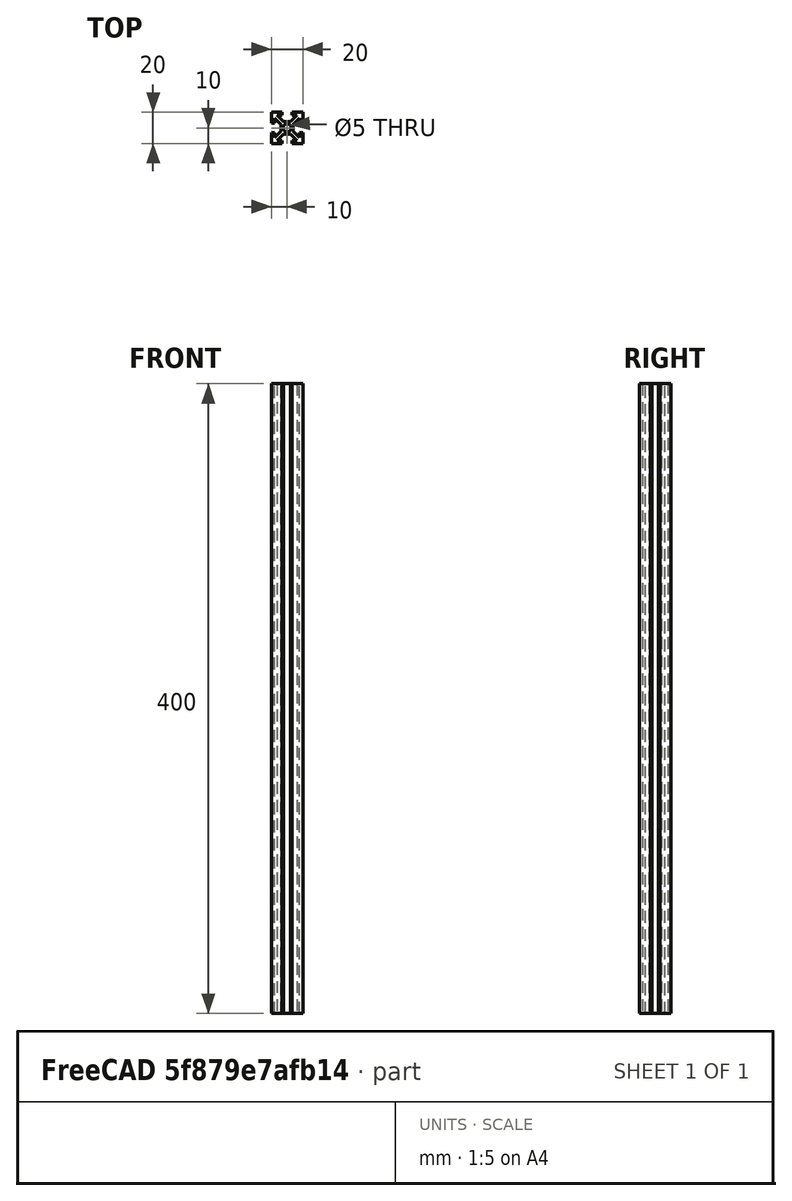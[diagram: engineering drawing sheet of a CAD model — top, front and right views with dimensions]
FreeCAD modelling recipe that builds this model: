
FCSTD DOCUMENT  (FreeCAD 1.0R39109 (Git))
Label: T-Slot_20_length
License: All rights reserved
LicenseURL: http://en.wikipedia.org/wiki/All_rights_reserved
objects: Sketcher::SketchObject×3, PartDesign::Pocket×2, TechDraw::DrawProjGroupItem×2, TechDraw::DrawViewDimension×2, PartDesign::Pad×1, PartDesign::Body×1, TechDraw::DrawSVGTemplate×1, TechDraw::DrawProjGroup×1, TechDraw::DrawPage×1
note: 19 computed .brp shape members not serialized (recipe doc carries the construction recipe); baked Part::Feature solids carry a one-line shape summary decoded from their .brp

FEATURE [Sketcher::SketchObject] Sketch
  ArcFitTolerance = 0
  AttachmentSupport = -> [XY_Plane]
  FullyConstrained = true
  MakeInternals = false
  MapMode = 5
  sketch-geometry (4):
    g0: LineSegment StartX=-10 StartY=10 StartZ=0 EndX=10 EndY=10 EndZ=0
    g1: LineSegment StartX=10 StartY=10 StartZ=0 EndX=10 EndY=-10 EndZ=0
    g2: LineSegment StartX=10 StartY=-10 StartZ=0 EndX=-10 EndY=-10 EndZ=0
    g3: LineSegment StartX=-10 StartY=-10 StartZ=0 EndX=-10 EndY=10 EndZ=0
  constraints (10):
    c: Coincident(g0,g1)
    c: Coincident(g1,g2)
    c: Coincident(g2,g3)
    c: Coincident(g3,g0)
    c: Horizontal(g0)
    c: Vertical(g1)
    c: Symmetric(g2,g1,g-2)
    c: Symmetric(g0,g2,g-1)
    c: Equal(g3,g2)
    c: Distance(g0) = 20
FEATURE [PartDesign::Pad] Pad  label="Change Length Here!"
  AllowMultiFace = false
  Direction = (0,0,1)
  Length = 400
  Length2 = 100
  Profile = -> Sketch
  ReferenceAxis = -> Sketch [N_Axis]
  Refine = true
  Suppressed = false
  Type = 0
FEATURE [Sketcher::SketchObject] Sketch001
  ArcFitTolerance = 0
  AttachmentSupport = -> [Pad]
  ExternalGeometry = -> [Pad]
  FullyConstrained = false
  MakeInternals = false
  MapMode = 5
  Placement = pos=(0,0,400) rot=(0,0,1;0rad)
  sketch-geometry (23):
    g0: LineSegment StartX=-3.1 StartY=10 StartZ=0 EndX=3.1 EndY=10 EndZ=0
    g1: LineSegment StartX=3.1 StartY=10 StartZ=0 EndX=3.1 EndY=8 EndZ=0
    g2: LineSegment [constr] StartX=3.1 StartY=8 StartZ=0 EndX=-3.1 EndY=8 EndZ=0
    g3: LineSegment StartX=-3.1 StartY=8 StartZ=0 EndX=-3.1 EndY=10 EndZ=0
    g4: LineSegment StartX=-3.1 StartY=8 StartZ=0 EndX=-6.23223 EndY=8 EndZ=0
    g5: LineSegment StartX=-6.23223 StartY=8 StartZ=0 EndX=-2.13223 EndY=3.9 EndZ=0
    g6: LineSegment StartX=-2.13223 StartY=3.9 StartZ=0 EndX=2.13223 EndY=3.9 EndZ=0
    g7: LineSegment StartX=2.13223 StartY=3.9 StartZ=0 EndX=6.23223 EndY=8 EndZ=0
    g8: LineSegment StartX=6.23223 StartY=8 StartZ=0 EndX=3.1 EndY=8 EndZ=0
    g9: LineSegment [constr] StartX=-3.9 StartY=3.9 StartZ=0 EndX=3.9 EndY=3.9 EndZ=0
    g10: LineSegment [constr] StartX=3.9 StartY=3.9 StartZ=0 EndX=3.9 EndY=-3.9 EndZ=0
    g11: LineSegment [constr] StartX=3.9 StartY=-3.9 StartZ=0 EndX=-3.9 EndY=-3.9 EndZ=0
    g12: LineSegment [constr] StartX=-3.9 StartY=-3.9 StartZ=0 EndX=-3.9 EndY=3.9 EndZ=0
    g13: Circle CenterX=0 CenterY=0 CenterZ=0 NormalX=0 NormalY=0 NormalZ=1 AngleXU=0 Radius=2.5
    g14: LineSegment [constr] StartX=3.9 StartY=3.9 StartZ=0 EndX=3.01612 EndY=4.78388 EndZ=0
    g15: LineSegment StartX=-3.1 StartY=-8 StartZ=0 EndX=-6.23223 EndY=-8 EndZ=0
    g16: LineSegment StartX=6.23223 StartY=-8 StartZ=0 EndX=3.1 EndY=-8 EndZ=0
    g17: LineSegment StartX=3.1 StartY=-10 StartZ=0 EndX=3.1 EndY=-8 EndZ=0
    g18: LineSegment StartX=-3.1 StartY=-10 StartZ=0 EndX=3.1 EndY=-10 EndZ=0
    g19: LineSegment StartX=-3.1 StartY=-8 StartZ=0 EndX=-3.1 EndY=-10 EndZ=0
    g20: LineSegment StartX=-6.23223 StartY=-8 StartZ=0 EndX=-2.13223 EndY=-3.9 EndZ=0
    g21: LineSegment StartX=-2.13223 StartY=-3.9 StartZ=0 EndX=2.13223 EndY=-3.9 EndZ=0
    g22: LineSegment StartX=2.13223 StartY=-3.9 StartZ=0 EndX=6.23223 EndY=-8 EndZ=0
  constraints (55):
    c: Coincident(g0,g1)
    c: Coincident(g1,g2)
    c: Coincident(g2,g3)
    c: Coincident(g3,g0)
    c: Horizontal(g2)
    c: Vertical(g1)
    c: Vertical(g3)
    c: PointOnObject(g0,g-3)
    c: Symmetric(g0,g0,g-2)
    c: Distance(g0) = 6.2
    c: Distance(g3) = 2
    c: Coincident(g3,g4)
    c: Horizontal(g4)
    c: Coincident(g4,g5)
    c: Coincident(g5,g6)
    c: Coincident(g6,g7)
    c: Coincident(g7,g8)
    c: Coincident(g8,g1)
    c: Horizontal(g8)
    c: Symmetric(g5,g6,g-2)
    c: Equal(g4,g8)
    c: Coincident(g9,g10)
    c: Coincident(g10,g11)
    c: Coincident(g11,g12)
    c: Coincident(g12,g9)
    c: Horizontal(g9)
    c: Vertical(g12)
    c: Equal(g9,g12)
    c: Symmetric(g11,g10,g-2)
    c: Symmetric(g9,g10,g-1)
    c: Distance(g9) = 7.8
    c: Coincident(g13,g-1)
    c: Radius(g13) = 2.5
    c: DistanceY(g6,g0) = 6.1
    c: Coincident(g14,g9)
    c: PointOnObject(g14,g7)
    c: Perpendicular(g7,g14)
    c: Distance(g14) = 1.25
    c: Angle(g6,g5) = 2.35619
    c: Coincident(g18,g17)
    c: Coincident(g19,g18)
    c: Vertical(g17)
    c: Vertical(g19)
    c: Distance(g18) = 6.2
    c: Distance(g19) = 2
    c: Coincident(g19,g15)
    c: Horizontal(g15)
    c: Coincident(g15,g20)
    c: Coincident(g20,g21)
    c: Coincident(g21,g22)
    c: Coincident(g22,g16)
    c: Coincident(g16,g17)
    c: Horizontal(g16)
    c: Equal(g15,g16)
    c: Angle(g21,g20) = -2.35619
FEATURE [PartDesign::Pocket] Pocket  label="Top & Bottom Slots"
  AllowMultiFace = false
  BaseFeature = -> Pad
  Direction = (0,0,-1)
  Length = 5
  Length2 = 100
  Profile = -> Sketch001
  Refine = true
  Suppressed = false
  Type = 1
FEATURE [Sketcher::SketchObject] Sketch002
  ArcFitTolerance = 0
  AttachmentSupport = -> [Pocket]
  ExternalGeometry = -> [Pocket]
  FullyConstrained = false
  MakeInternals = false
  MapMode = 5
  Placement = pos=(0,0,0) rot=(1,0,0;3.14159rad)
  sketch-geometry (19):
    g0: LineSegment StartX=-10 StartY=-3.1 StartZ=0 EndX=-8 EndY=-3.1 EndZ=0
    g1: LineSegment [constr] StartX=-8 StartY=-3.1 StartZ=0 EndX=-8 EndY=3.1 EndZ=0
    g2: LineSegment StartX=-8 StartY=3.1 StartZ=0 EndX=-10 EndY=3.1 EndZ=0
    g3: LineSegment StartX=-10 StartY=3.1 StartZ=0 EndX=-10 EndY=-3.1 EndZ=0
    g4: LineSegment StartX=-8 StartY=-3.1 StartZ=0 EndX=-8 EndY=-6.23223 EndZ=0
    g5: LineSegment StartX=-8 StartY=-6.23223 StartZ=0 EndX=-3.9 EndY=-2.13223 EndZ=0
    g6: LineSegment StartX=-3.9 StartY=-2.13223 StartZ=0 EndX=-3.9 EndY=2.13223 EndZ=0
    g7: LineSegment StartX=-3.9 StartY=2.13223 StartZ=0 EndX=-8 EndY=6.23223 EndZ=0
    g8: LineSegment StartX=-8 StartY=6.23223 StartZ=0 EndX=-8 EndY=3.1 EndZ=0
    g9: LineSegment [constr] StartX=-2.13223 StartY=3.9 StartZ=0 EndX=-3.9 EndY=2.13223 EndZ=0
    g10: LineSegment [constr] StartX=2.13223 StartY=3.9 StartZ=0 EndX=3.9 EndY=2.13223 EndZ=0
    g11: LineSegment StartX=3.9 StartY=-2.13223 StartZ=0 EndX=3.9 EndY=2.13223 EndZ=0
    g12: LineSegment StartX=8 StartY=-6.23223 StartZ=0 EndX=3.9 EndY=-2.13223 EndZ=0
    g13: LineSegment StartX=3.9 StartY=2.13223 StartZ=0 EndX=8 EndY=6.23223 EndZ=0
    g14: LineSegment StartX=8 StartY=6.23223 StartZ=0 EndX=8 EndY=3.1 EndZ=0
    g15: LineSegment StartX=8 StartY=3.1 StartZ=0 EndX=10 EndY=3.1 EndZ=0
    g16: LineSegment StartX=10 StartY=3.1 StartZ=0 EndX=10 EndY=-3.1 EndZ=0
    g17: LineSegment StartX=10 StartY=-3.1 StartZ=0 EndX=8 EndY=-3.1 EndZ=0
    g18: LineSegment StartX=8 StartY=-3.1 StartZ=0 EndX=8 EndY=-6.23223 EndZ=0
  constraints (43):
    c: Coincident(g0,g1)
    c: Coincident(g1,g2)
    c: Coincident(g2,g3)
    c: Coincident(g3,g0)
    c: Horizontal(g0)
    c: Horizontal(g2)
    c: Vertical(g1)
    c: PointOnObject(g0,g-3)
    c: Symmetric(g2,g0,g-1)
    c: Distance(g3) = 6.2
    c: Distance(g0) = 2
    c: Coincident(g0,g4)
    c: Vertical(g4)
    c: Coincident(g4,g5)
    c: Coincident(g5,g6)
    c: Coincident(g6,g7)
    c: Coincident(g7,g8)
    c: Coincident(g8,g2)
    c: Vertical(g8)
    c: Equal(g4,g8)
    c: Symmetric(g6,g5,g-1)
    c: DistanceX(g2,g6) = 6.1
    c: Angle(g6,g5) = 2.35619
    c: Coincident(g9,g-4)
    c: Perpendicular(g-4,g9)
    c: Coincident(g6,g9)
    c: Coincident(g15,g16)
    c: Coincident(g16,g17)
    c: Horizontal(g17)
    c: Horizontal(g15)
    c: Distance(g16) = 6.2
    c: Distance(g17) = 2
    c: Coincident(g17,g18)
    c: Vertical(g18)
    c: Coincident(g18,g12)
    c: Coincident(g12,g11)
    c: Coincident(g11,g13)
    c: Coincident(g13,g14)
    c: Coincident(g14,g15)
    c: Vertical(g14)
    c: Equal(g18,g14)
    c: Angle(g11,g12) = -2.35619
    c: Coincident(g11,g10)
FEATURE [PartDesign::Pocket] Pocket001  label="R&L Slots"
  AllowMultiFace = false
  BaseFeature = -> Pocket
  Direction = (0,0,1)
  Length = 5
  Length2 = 100
  Profile = -> Sketch002
  Refine = true
  Suppressed = false
  Type = 1
FEATURE [PartDesign::Body] Body  label="Tslot20_len"
  AllowCompound = false
  Group = -> [Sketch,Pad,Sketch001,Pocket,Sketch002,Pocket001]
  Origin = -> Origin
  Tip = -> Pocket001
FEATURE [TechDraw::DrawSVGTemplate] Template
  EditableTexts = approval_person=B. Hecate; creator=Djordje Vujic; date_of_issue=1/21/2025; document_type=Assembly Drawing; general_tolerances=ISO 2768-m; identification_number=DN; language_code=EN; part_material=Stainless steel Mat.No. 1.4301; revision_index=AAA; sheet_number=1 / 5; sheet_scale=1 : 2; title=T-Slot_20_length
  Height = 297
  Orientation = 0
  Template = D:/Program Files/FreeCAD 1.0/data/Mod/TechDraw/Templates/A4_Portrait_ISO5457_minimal.svg
  Width = 210
FEATURE [TechDraw::DrawProjGroupItem] ProjItem  label="Front"
  CoarseView = false
  Direction = (0,-1,0)
  Focus = 100
  HardHidden = false
  IsoCount = 0
  IsoHidden = false
  IsoVisible = false
  LockPosition = true
  Perspective = false
  Rotation = 0
  RotationVector = (1,0,0)
  Scale = 0.5
  ScaleType = 0
  ScrubCount = 1
  SeamHidden = false
  SeamVisible = false
  SmoothHidden = false
  SmoothVisible = true
  Source = -> [Body]
  Type = 0
  X = 0
  XDirection = (1,0,0)
  Y = 0
FEATURE [TechDraw::DrawProjGroupItem] ProjItem001  label="Bottom"
  CoarseView = false
  Direction = (0,0,-1)
  Focus = 100
  HardHidden = false
  IsoCount = 0
  IsoHidden = false
  IsoVisible = false
  LockPosition = false
  Perspective = false
  Rotation = 0
  RotationVector = (1,0,0)
  Scale = 0.5
  ScaleType = 0
  ScrubCount = 1
  SeamHidden = false
  SeamVisible = false
  SmoothHidden = false
  SmoothVisible = true
  Source = -> [Body]
  Type = 5
  X = 0
  XDirection = (1,0,0)
  Y = 120
FEATURE [TechDraw::DrawProjGroup] ProjGroup
  Anchor = -> ProjItem
  AutoDistribute = true
  LockPosition = false
  ProjectionType = 0
  Rotation = 0
  Scale = 0.5
  ScaleType = 2
  Source = -> [Body]
  Views = -> [ProjItem,ProjItem001]
  X = 104.931
  Y = 160.059
  spacingX = 15
  spacingY = 15
FEATURE [TechDraw::DrawViewDimension] Dimension
  AngleOverride = false
  Arbitrary = false
  ArbitraryTolerances = false
  BoxCorners = (2) [(-5,-100,0),(5,100,0)]
  EqualTolerance = true
  ExtensionAngle = 0
  FormatSpec = %.2w
  FormatSpecOverTolerance = %+.2w
  FormatSpecUnderTolerance = %+.2w
  Inverted = false
  LineAngle = 0
  LockPosition = false
  MeasureType = 1
  OverTolerance = 0
  References2D = -> [ProjItem]
  Rotation = 0
  ScaleType = 0
  TheoreticalExact = false
  Type = 2
  UnderTolerance = 0
  X = 24.0453
  Y = -12.9531
FEATURE [TechDraw::DrawViewDimension] Dimension001
  AngleOverride = false
  Arbitrary = false
  ArbitraryTolerances = false
  BoxCorners = (2) [(-5,-5,0),(5,5,0)]
  EqualTolerance = true
  ExtensionAngle = 0
  FormatSpec = %.2w
  FormatSpecOverTolerance = %+.2w
  FormatSpecUnderTolerance = %+.2w
  Inverted = false
  LineAngle = 0
  LockPosition = false
  MeasureType = 1
  OverTolerance = 0
  References2D = -> [ProjItem001]
  Rotation = 0
  ScaleType = 0
  TheoreticalExact = false
  Type = 2
  UnderTolerance = 0
  X = 23.5343
  Y = -10.7172
FEATURE [TechDraw::DrawPage] Page
  KeepUpdated = true
  NextBalloonIndex = 1
  ProjectionType = 0
  Template = -> Template
  Views = -> [ProjGroup,Dimension,Dimension001]
